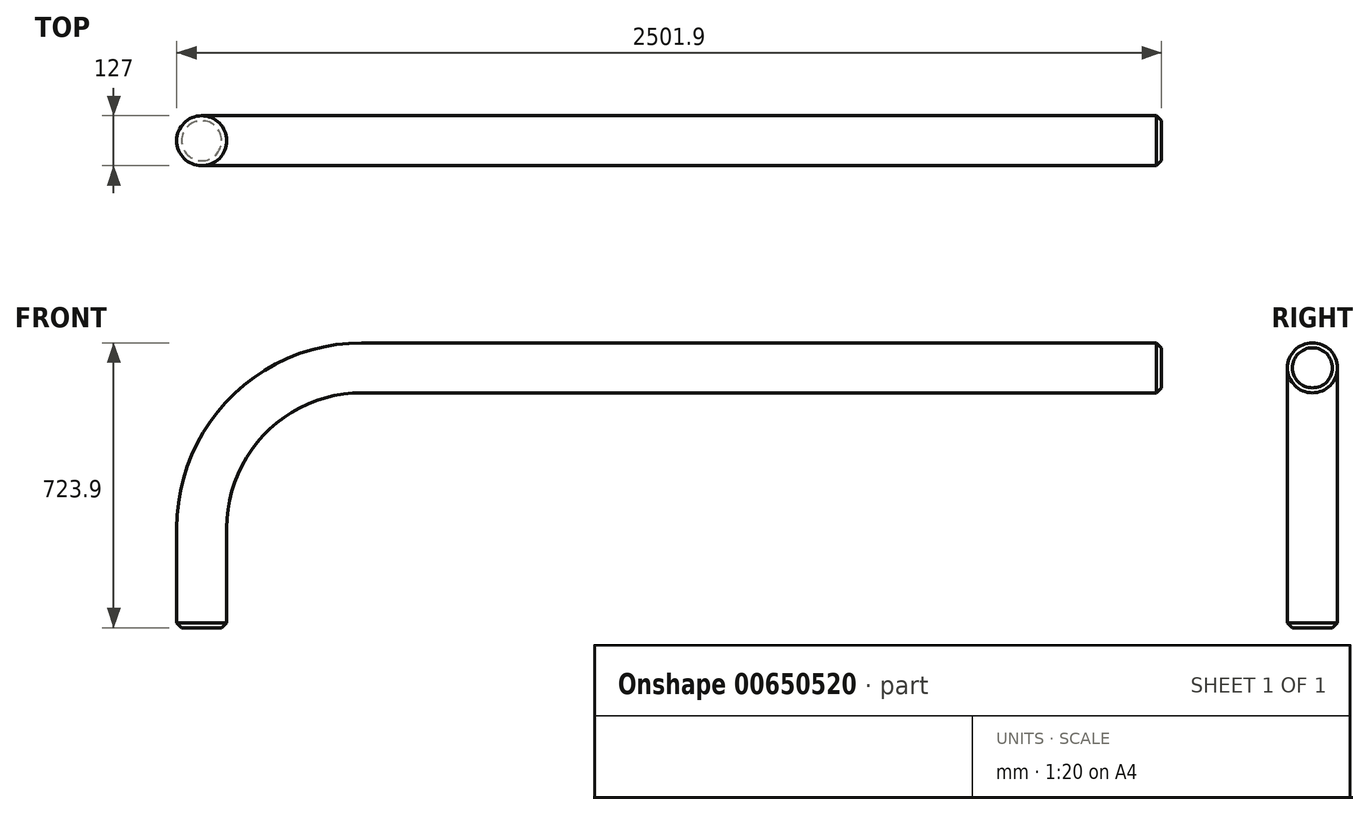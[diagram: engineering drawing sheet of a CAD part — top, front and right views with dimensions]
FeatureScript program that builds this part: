
annotation { "Feature Type Name" : "Feature", "Feature Type Description" : "" }
export const myFeature = defineFeature(function(context is Context, id is Id, definition is map)
    precondition{}
    {
        {
            var Q0;
            Q0=qCreatedBy(makeId("Front.planeOp"),FACE);
            var sketch = newSketch(context, id + "F0", { "sketchPlane" : qUnion([Q0])});
            skLineSegment(sketch, "E0", {"start": v(0, 375.18) * mm, "end": v(-2032, 375.18) * mm});
            skLineSegment(sketch, "E1", {"start": v(-2438.4, -31.22) * mm, "end": v(-2438.4, -285.22) * mm});
            skPoint(sketch, "E2.visualSharp", {"position": v(-2438.4, 375.18) * mm});
            skArc(sketch, "E2.filletArc", {"start": v(-2032, 375.18) * mm, "mid": v(-2319.37, 256.15) * mm, "end": v(-2438.4, -31.22) * mm});
            skSolve(sketch);
        }
        {
            var Q0;
            Q0=qCreatedBy(makeId("Right.planeOp"),FACE);
            var sketch = newSketch(context, id + "F1", { "sketchPlane" : qUnion([Q0])});
            skCircle(sketch, "E3", {"center": v(0, 375.18) * mm, "radius": 63.5 * mm});
            skSolve(sketch);
        }
        {
            var Q0;
            Q0=makeQuery(id+"F1.imprint","IMPRINT",FACE,{"disambiguationData":[TD([[makeQuery(id+"F1.imprint","IMPRINT",EDGE,{"derivedFrom":sQuery(id+"F1.wireOp",EDGE,"E3")}),1.0]])]});
            var Q1;
            Q1=sQuery(id+"F0.wireOp",EDGE,"E0");
            var Q2;
            Q2=sQuery(id+"F0.wireOp",EDGE,"E2.filletArc");
            var Q3;
            Q3=sQuery(id+"F0.wireOp",EDGE,"E1");
            sweep(context, id + "F2", {"profiles" : qUnion([Q0]), "path" : qUnion([Q1, Q2, Q3])});
        }
        {
            var Q0;
            Q0=makeQuery(id+"F2.opSweep","CAP_EDGE",EDGE,{"disambiguationData":[OSD([sQuery(id+"F0.wireOp",VERTEX,"E0.start"),sQuery(id+"F1.wireOp",EDGE,"E3")])],"isStart":true});
            var Q1;
            Q1=makeQuery(id+"F2.opSweep","CAP_EDGE",EDGE,{"disambiguationData":[OSD([sQuery(id+"F0.wireOp",VERTEX,"E1.end"),sQuery(id+"F1.wireOp",EDGE,"E3")])],"isStart":false});
            chamfer(context, id + "F3", {"entities" : qUnion([Q0, Q1]), "chamferType" : ChamferType.OFFSET_ANGLE, "width" : 12.7 * mm, "oppositeDirection" : false, "angle" : 45 * degree, "tangentPropagation" : true});
        }
    });
